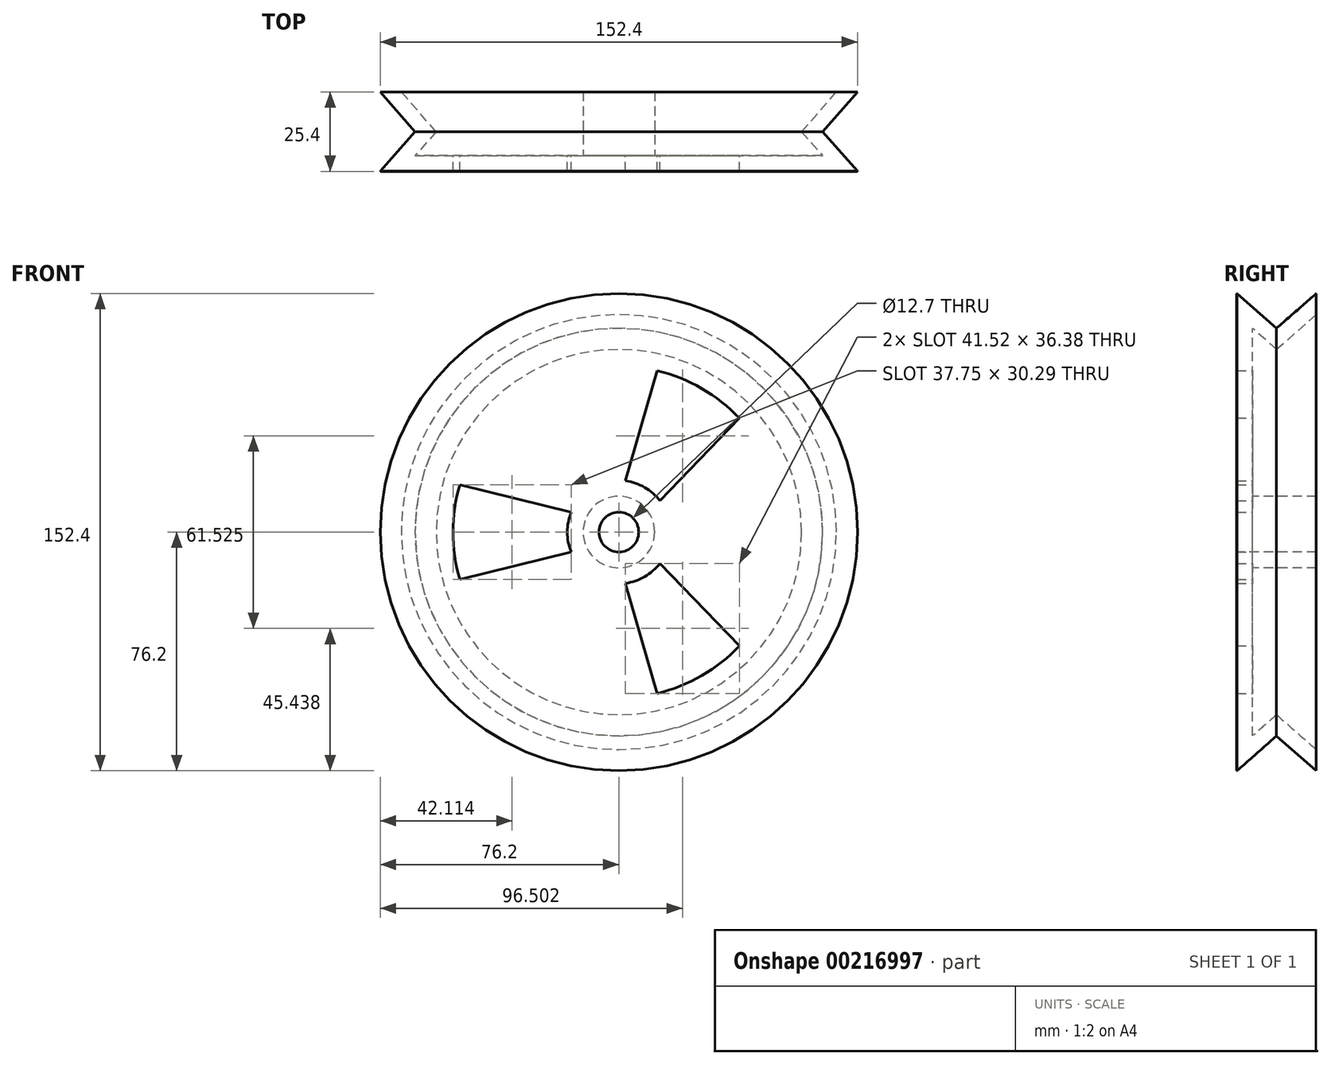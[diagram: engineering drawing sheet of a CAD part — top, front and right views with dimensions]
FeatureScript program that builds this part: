
annotation { "Feature Type Name" : "Feature", "Feature Type Description" : "" }
export const myFeature = defineFeature(function(context is Context, id is Id, definition is map)
    precondition{}
    {
        {
            var Q0;
            Q0=qCreatedBy(makeId("Front.planeOp"),FACE);
            var sketch = newSketch(context, id + "F0", { "sketchPlane" : qUnion([Q0])});
            skCircle(sketch, "E0", {"center": v(0, 0) * mm, "radius": 76.2 * mm});
            skSolve(sketch);
        }
        {
            var Q0;
            Q0 = qSketchRegion(id + "F0", true);
            extrude(context, id + "F1", {"entities" : qUnion([Q0]), "depth" : 25.4 * mm});
        }
        {
            var Q0;
            Q0=qCreatedBy(makeId("Right.planeOp"),FACE);
            var sketch = newSketch(context, id + "F2", { "sketchPlane" : qUnion([Q0])});
            skLineSegment(sketch, "E1", {"start": v(0, 76.23) * mm, "end": v(-12.7, 76.23) * mm});
            skLineSegment(sketch, "E2", {"start": v(0, 76.23) * mm, "end": v(-12.7, 65.11) * mm});
            skLineSegment(sketch, "E3", {"start": v(-12.7, 65.11) * mm, "end": v(-25.3, 76.23) * mm});
            skLineSegment(sketch, "E4", {"start": v(-25.3, 76.23) * mm, "end": v(0, 76.23) * mm});
            skSolve(sketch);
        }
        {
            var Q0;
            Q0 = qSketchRegion(id + "F2", true);
            var Q1;
            Q1=makeQuery(id+"F1.opExtrude","CAP_EDGE",EDGE,{"disambiguationData":[OSD([sQuery(id+"F0.wireOp",EDGE,"E0")])],"isStart":false});
            revolve(context, id + "F3", {"operationType" : NewBodyOperationType.REMOVE, "entities" : qUnion([Q0]), "axis" : qUnion([Q1]), "revolveType" : RevolveType.FULL, "oppositeDirection" : true});
        }
        {
            var Q0;
            Q0=makeQuery(id+"F1.opExtrude","CAP_FACE",FACE,{"disambiguationData":[OSD([sQuery(id+"F0.wireOp",EDGE,"E0")])],"isStart":false});
            var sketch = newSketch(context, id + "F4", { "sketchPlane" : qUnion([Q0])});
            skCircle(sketch, "E5", {"center": v(0, 0) * mm, "radius": 6.35 * mm});
            skSolve(sketch);
        }
        {
            var Q0;
            Q0 = qSketchRegion(id + "F4", true);
            extrude(context, id + "F5", {"entities" : qUnion([Q0]), "operationType" : NewBodyOperationType.REMOVE, "oppositeDirection" : true, "depth" : 25.4 * mm});
        }
        {
            var Q0;
            Q0=makeQuery(id+"F1.opExtrude","CAP_FACE",FACE,{"disambiguationData":[OSD([sQuery(id+"F0.wireOp",EDGE,"E0")])],"isStart":true});
            shell(context, id + "F6", {"entities" : qUnion([Q0]), "thickness" : 5.08 * mm});
        }
        {
            var Q0;
            {var subQ0=sQuery(id+"F0.wireOp",EDGE,"E0");Q0=makeQuery(id+"F6.opShell","OFFSET_FACE",FACE,{"disambiguationData":[OSD([subQ0]),TDD([makeQuery(id+"F1.opExtrude","CAP_FACE",FACE,{"disambiguationData":[OSD([subQ0])],"isStart":false})])]});}
            var sketch = newSketch(context, id + "F7", { "sketchPlane" : qUnion([Q0])});
            skCircle(sketch, "E6", {"center": v(0, 0) * mm, "radius": 52.96 * mm});
            skCircle(sketch, "E7", {"center": v(0, 0) * mm, "radius": 16.48 * mm});
            skLineSegment(sketch, "E8", {"start": v(50.75, 15.15) * mm, "end": v(15.2, 6.34) * mm});
            skLineSegment(sketch, "E9.MirrorCS", {"start": v(50.75, -15.15) * mm, "end": v(15.2, -6.34) * mm});
            skPoint(sketch, "E10.start.orphan", {"position": v(16.48, 0) * mm});
            skLineSegment(sketch, "E11.1.0", {"start": v(-12.26, 51.52) * mm, "end": v(-2.11, 16.34) * mm});
            skLineSegment(sketch, "E11.1.1", {"start": v(-38.5, 36.38) * mm, "end": v(-13.1, 10) * mm});
            skLineSegment(sketch, "E11.2.0", {"start": v(-38.5, -36.38) * mm, "end": v(-13.1, -10) * mm});
            skLineSegment(sketch, "E11.2.1", {"start": v(-12.26, -51.52) * mm, "end": v(-2.11, -16.34) * mm});
            skSolve(sketch);
        }
        {
            var Q0;
            {var subQ0=sQuery(id+"F7.wireOp",EDGE,"E8");Q0=makeQuery(id+"F7.imprint","IMPRINT",FACE,{"disambiguationData":[TD([[makeQuery(id+"F7.imprint","IMPRINT",EDGE,{"derivedFrom":subQ0}),1.0]])]});}
            var Q1;
            {var subQ0=sQuery(id+"F7.wireOp",EDGE,"E11.2.0");Q1=makeQuery(id+"F7.imprint","IMPRINT",FACE,{"disambiguationData":[TD([[makeQuery(id+"F7.imprint","IMPRINT",EDGE,{"derivedFrom":subQ0}),-1.0]])]});}
            var Q2;
            {var subQ0=sQuery(id+"F7.wireOp",EDGE,"E11.1.0");Q2=makeQuery(id+"F7.imprint","IMPRINT",FACE,{"disambiguationData":[TD([[makeQuery(id+"F7.imprint","IMPRINT",EDGE,{"derivedFrom":subQ0}),-1.0]])]});}
            extrude(context, id + "F8", {"entities" : qUnion([Q0, Q1, Q2]), "operationType" : NewBodyOperationType.REMOVE, "endBound" : BoundingType.THROUGH_ALL, "oppositeDirection" : true, "depth" : 25.4 * mm});
        }
    });
